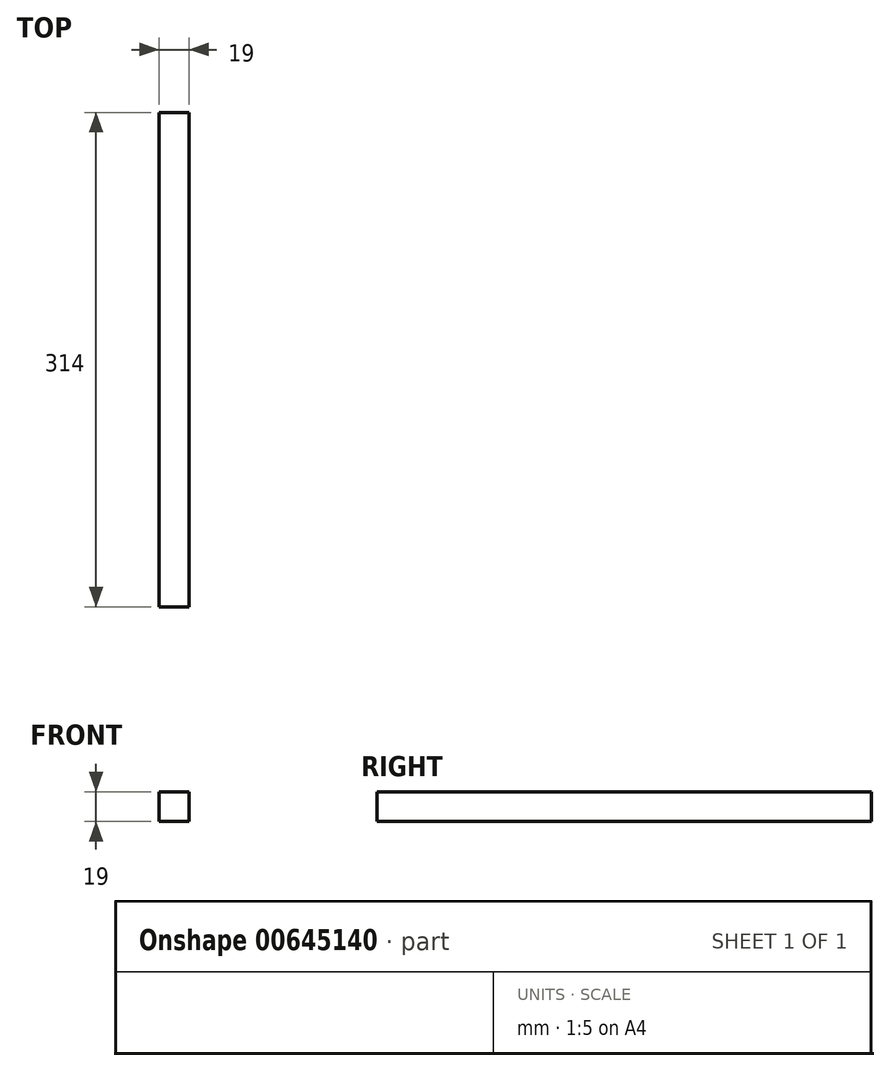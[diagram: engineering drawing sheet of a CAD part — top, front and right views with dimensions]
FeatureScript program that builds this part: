
annotation { "Feature Type Name" : "Feature", "Feature Type Description" : "" }
export const myFeature = defineFeature(function(context is Context, id is Id, definition is map)
    precondition{}
    {
        {
            var Q0;
            Q0=qCreatedBy(makeId("Front.planeOp"),FACE);
            var sketch = newSketch(context, id + "F0", { "sketchPlane" : qUnion([Q0])});
            skLineSegment(sketch, "E0.bottom", {"start": v(9.5, -9.5) * mm, "end": v(-9.5, -9.5) * mm});
            skLineSegment(sketch, "E0.top", {"start": v(9.5, 9.5) * mm, "end": v(-9.5, 9.5) * mm});
            skLineSegment(sketch, "E0.left", {"start": v(9.5, -9.5) * mm, "end": v(9.5, 9.5) * mm});
            skLineSegment(sketch, "E0.right", {"start": v(-9.5, -9.5) * mm, "end": v(-9.5, 9.5) * mm});
            skPoint(sketch, "E0.middle", {"position": v(0, 0) * mm});
            skSolve(sketch);
        }
        {
            var Q0;
            Q0=makeQuery(id+"F0.imprint","IMPRINT",FACE,{"disambiguationData":[TD([[makeQuery(id+"F0.imprint","IMPRINT",EDGE,{"derivedFrom":sQuery(id+"F0.wireOp",EDGE,"E0.bottom")}),-1.0]])]});
            extrude(context, id + "F1", {"entities" : qUnion([Q0]), "endBound" : BoundingType.SYMMETRIC, "depth" : (314) * mm, "offsetDistance" : 25.4 * mm});
        }
    });
